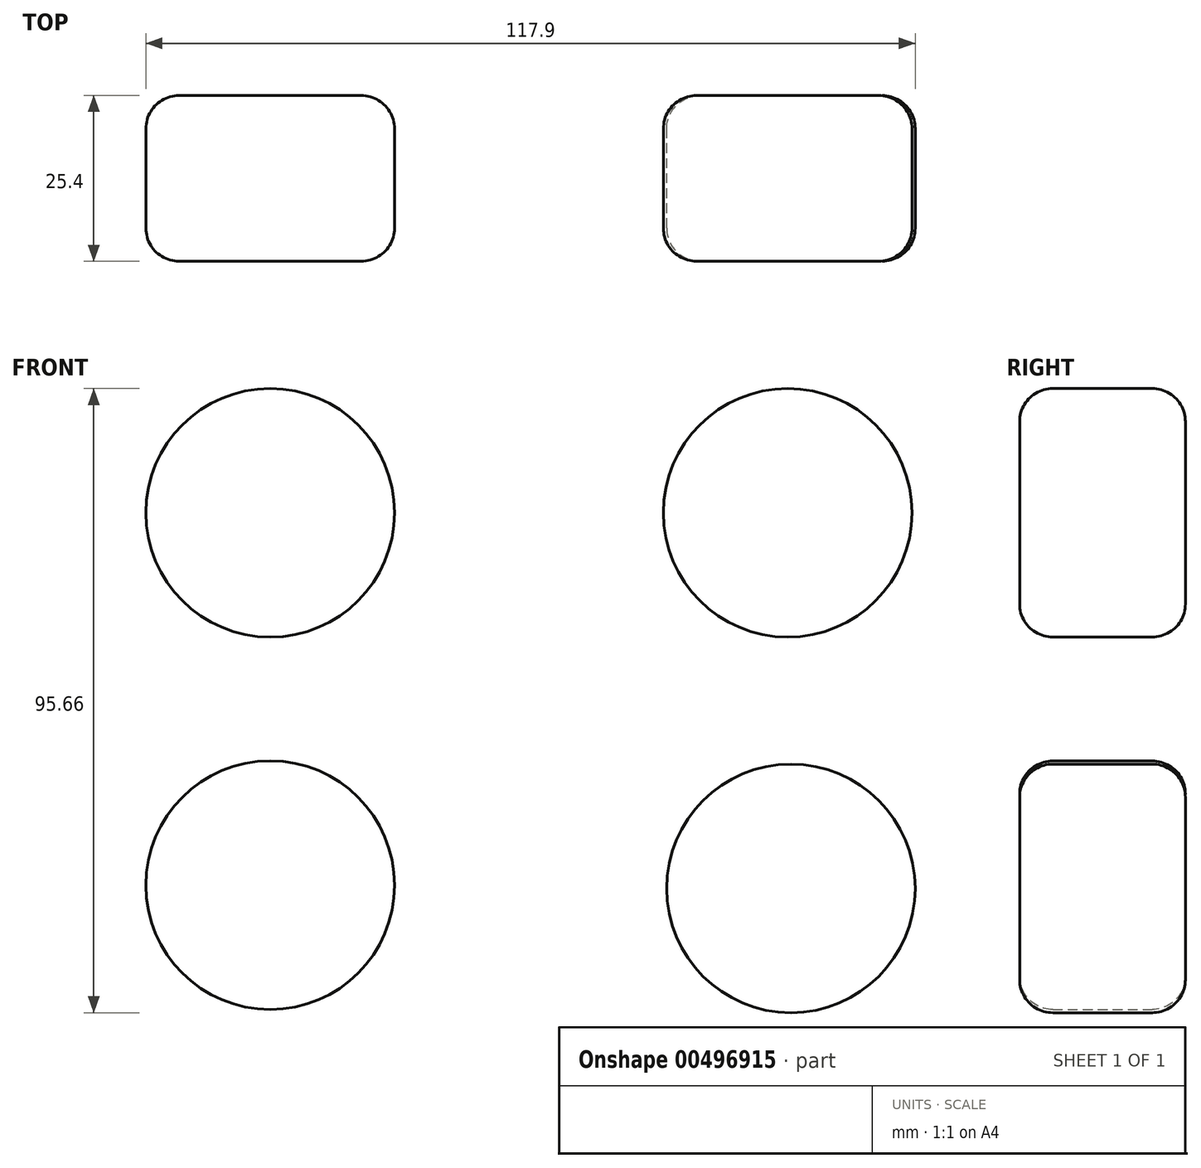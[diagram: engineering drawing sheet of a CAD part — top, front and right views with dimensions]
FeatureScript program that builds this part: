
annotation { "Feature Type Name" : "Feature", "Feature Type Description" : "" }
export const myFeature = defineFeature(function(context is Context, id is Id, definition is map)
    precondition{}
    {
        {
            var Q0;
            Q0=qCreatedBy(makeId("Front.planeOp"),FACE);
            var sketch = newSketch(context, id + "F0", { "sketchPlane" : qUnion([Q0])});
            skCircle(sketch, "E0", {"center": v(-40.02, 30.4) * mm, "radius": 19.05 * mm});
            skCircle(sketch, "E1", {"center": v(39.29, 30.4) * mm, "radius": 19.05 * mm});
            skCircle(sketch, "E2", {"center": v(39.78, -27.17) * mm, "radius": 19.05 * mm});
            skCircle(sketch, "E3", {"center": v(-40.02, -26.68) * mm, "radius": 19.05 * mm});
            skSolve(sketch);
        }
        {
            var Q0;
            Q0=makeQuery(id+"F0.imprint","IMPRINT",FACE,{"disambiguationData":[TD([[makeQuery(id+"F0.imprint","IMPRINT",EDGE,{"derivedFrom":sQuery(id+"F0.wireOp",EDGE,"E0")}),1.0]])]});
            var Q1;
            Q1=makeQuery(id+"F0.imprint","IMPRINT",FACE,{"disambiguationData":[TD([[makeQuery(id+"F0.imprint","IMPRINT",EDGE,{"derivedFrom":sQuery(id+"F0.wireOp",EDGE,"E1")}),1.0]])]});
            var Q2;
            Q2=makeQuery(id+"F0.imprint","IMPRINT",FACE,{"disambiguationData":[TD([[makeQuery(id+"F0.imprint","IMPRINT",EDGE,{"derivedFrom":sQuery(id+"F0.wireOp",EDGE,"E3")}),1.0]])]});
            var Q3;
            Q3=makeQuery(id+"F0.imprint","IMPRINT",FACE,{"disambiguationData":[TD([[makeQuery(id+"F0.imprint","IMPRINT",EDGE,{"derivedFrom":sQuery(id+"F0.wireOp",EDGE,"E2")}),1.0]])]});
            extrude(context, id + "F1", {"entities" : qUnion([Q0, Q1, Q2, Q3]), "depth" : 25.4 * mm});
        }
        {
            var Q0;
            Q0=makeQuery(id+"F1.opExtrude","CAP_FACE",FACE,{"disambiguationData":[OSD([sQuery(id+"F0.wireOp",EDGE,"E0")])],"isStart":false});
            var Q1;
            Q1=makeQuery(id+"F1.opExtrude","CAP_FACE",FACE,{"disambiguationData":[OSD([sQuery(id+"F0.wireOp",EDGE,"E1")])],"isStart":false});
            var Q2;
            Q2=makeQuery(id+"F1.opExtrude","CAP_FACE",FACE,{"disambiguationData":[OSD([sQuery(id+"F0.wireOp",EDGE,"E3")])],"isStart":false});
            var Q3;
            Q3=makeQuery(id+"F1.opExtrude","CAP_FACE",FACE,{"disambiguationData":[OSD([sQuery(id+"F0.wireOp",EDGE,"E2")])],"isStart":false});
            fillet(context, id + "F2", {"entities" : qUnion([Q0, Q1, Q2, Q3]), "radius" : 5.08 * mm, "tangentPropagation" : true, "allowEdgeOverflow" : false});
        }
        {
            var Q0;
            Q0=makeQuery(id+"F1.opExtrude","CAP_FACE",FACE,{"disambiguationData":[OSD([sQuery(id+"F0.wireOp",EDGE,"E3")])],"isStart":true});
            var Q1;
            Q1=makeQuery(id+"F1.opExtrude","CAP_FACE",FACE,{"disambiguationData":[OSD([sQuery(id+"F0.wireOp",EDGE,"E2")])],"isStart":true});
            var Q2;
            Q2=makeQuery(id+"F1.opExtrude","CAP_FACE",FACE,{"disambiguationData":[OSD([sQuery(id+"F0.wireOp",EDGE,"E0")])],"isStart":true});
            fillet(context, id + "F3", {"entities" : qUnion([Q0, Q1, Q2]), "radius" : 5.08 * mm, "tangentPropagation" : true, "allowEdgeOverflow" : false});
        }
        {
            var Q0;
            Q0=makeQuery(id+"F1.opExtrude","CAP_FACE",FACE,{"disambiguationData":[OSD([sQuery(id+"F0.wireOp",EDGE,"E1")])],"isStart":true});
            fillet(context, id + "F4", {"entities" : qUnion([Q0]), "radius" : 5.08 * mm, "tangentPropagation" : true, "allowEdgeOverflow" : false});
        }
    });
